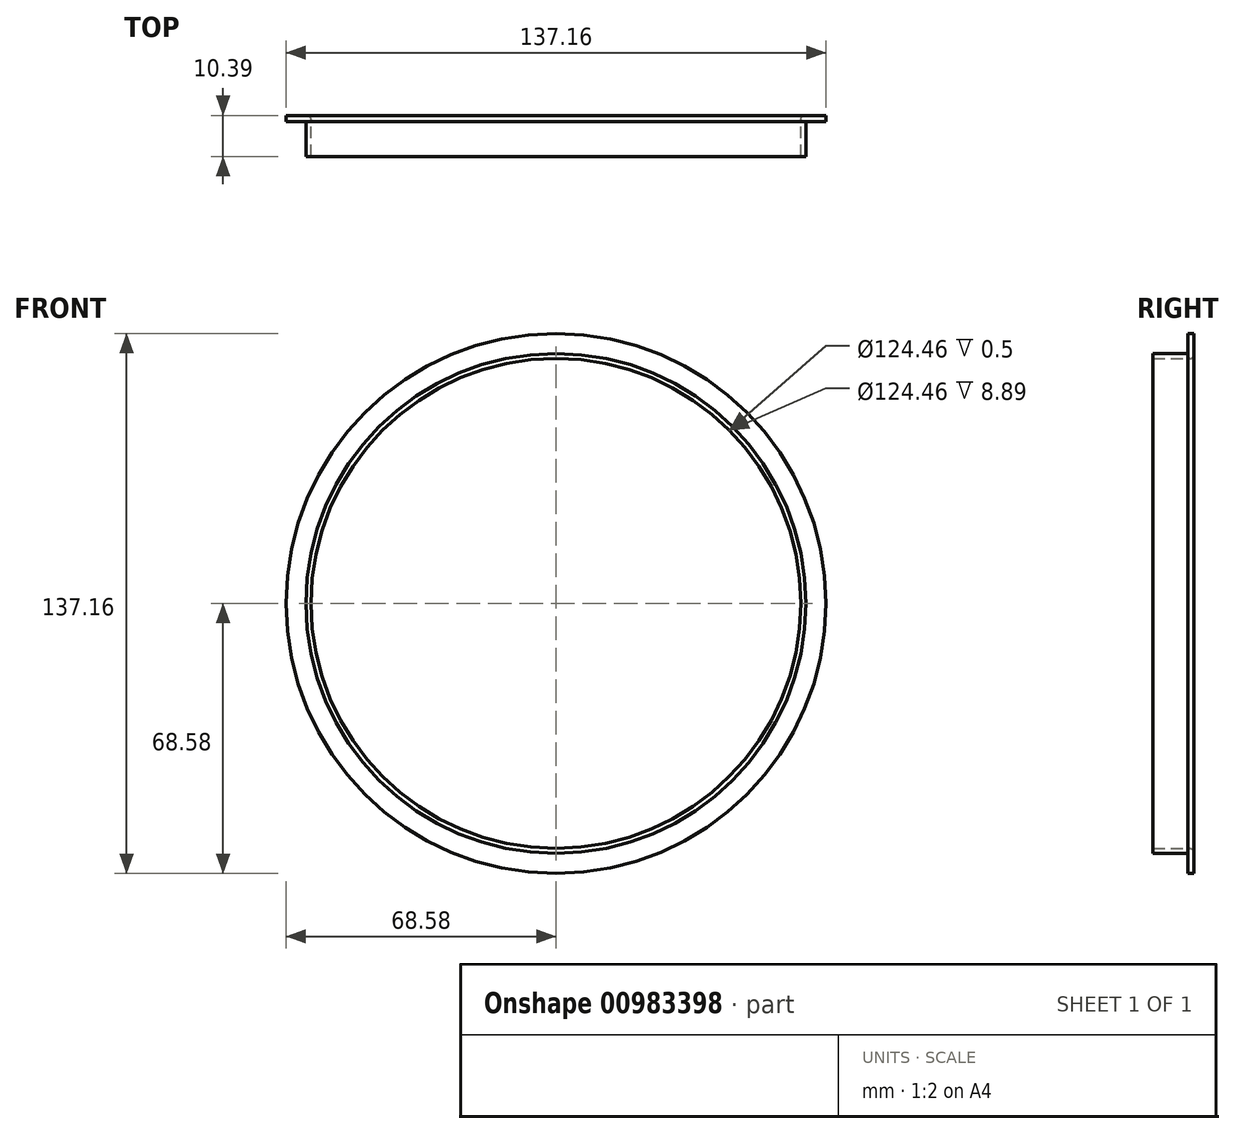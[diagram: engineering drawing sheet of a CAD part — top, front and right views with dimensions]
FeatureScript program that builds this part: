
annotation { "Feature Type Name" : "Feature", "Feature Type Description" : "" }
export const myFeature = defineFeature(function(context is Context, id is Id, definition is map)
    precondition{}
    {
        {
            var Q0;
            Q0=qCreatedBy(makeId("Front.planeOp"),FACE);
            var sketch = newSketch(context, id + "F0", { "sketchPlane" : qUnion([Q0])});
            skCircle(sketch, "E0", {"center": v(0, 0) * mm, "radius": 63.5 * mm});
            skCircle(sketch, "E1", {"center": v(0, 0) * mm, "radius": 62.23 * mm});
            skSolve(sketch);
        }
        {
            var Q0;
            Q0 = qSketchRegion(id + "F0", true);
            extrude(context, id + "F1", {"entities" : qUnion([Q0]), "depth" : 8.9 * mm, "offsetDistance" : 25.4 * mm});
        }
        {
            var Q0;
            Q0=qCreatedBy(makeId("Front.planeOp"),FACE);
            var sketch = newSketch(context, id + "F2", { "sketchPlane" : qUnion([Q0])});
            skCircle(sketch, "E2", {"center": v(0, 0) * mm, "radius": 68.58 * mm});
            skCircle(sketch, "E3", {"center": v(0, 0) * mm, "radius": 62.23 * mm});
            skSolve(sketch);
        }
        {
            var Q0;
            Q0 = qSketchRegion(id + "F2", true);
            extrude(context, id + "F3", {"entities" : qUnion([Q0]), "oppositeDirection" : true, "depth" : 1.5 * mm, "offsetDistance" : 25.4 * mm});
        }
        {
            var Q0;
            Q0=makeQuery(id+"F3.opExtrude","CAP_EDGE",EDGE,{"disambiguationData":[OSD([sQuery(id+"F2.wireOp",EDGE,"E3")])],"isStart":false});
            fillet(context, id + "F4", {"entities" : qUnion([Q0]), "radius" : 1 * mm, "tangentPropagation" : true, "allowEdgeOverflow" : false});
        }
    });
